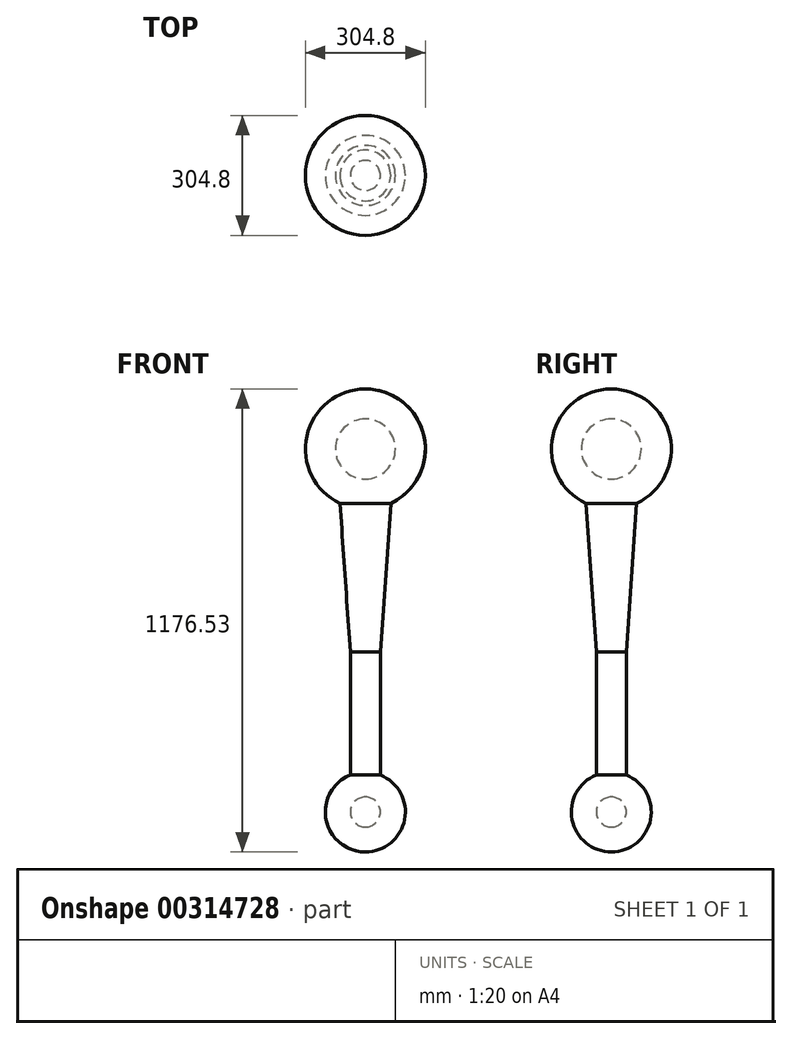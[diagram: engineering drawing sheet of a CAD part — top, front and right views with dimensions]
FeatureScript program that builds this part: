
annotation { "Feature Type Name" : "Feature", "Feature Type Description" : "" }
export const myFeature = defineFeature(function(context is Context, id is Id, definition is map)
    precondition{}
    {
        {
            var Q0;
            Q0=qCreatedBy(makeId("Front.planeOp"),FACE);
            var sketch = newSketch(context, id + "F0", { "sketchPlane" : qUnion([Q0])});
            skLineSegment(sketch, "E0", {"start": v(37.66, 184.96) * mm, "end": v(37.66, -183.34) * mm});
            skCircle(sketch, "E1", {"center": v(37.66, -221.44) * mm, "radius": 38.1 * mm});
            skLineSegment(sketch, "E2.0", {"start": v(75.76, 184.96) * mm, "end": v(75.76, -127.25) * mm});
            skArc(sketch, "E3", {"start": v(102.16, 563.01) * mm, "mid": v(186.44, 734.12) * mm, "end": v(37.66, 853.49) * mm});
            skCircle(sketch, "E4", {"center": v(37.66, 701.09) * mm, "radius": 76.2 * mm});
            skLineSegment(sketch, "E5", {"start": v(37.66, -259.54) * mm, "end": v(37.66, -323.04) * mm});
            skArc(sketch, "E6.trimOffspring", {"start": v(37.66, -323.04) * mm, "mid": v(137.39, -240.84) * mm, "end": v(75.76, -127.25) * mm});
            skLineSegment(sketch, "E7.trimOffspring", {"start": v(102.16, 563.01) * mm, "end": v(75.76, 184.96) * mm});
            skLineSegment(sketch, "E8.trimOffspring", {"start": v(37.66, 777.29) * mm, "end": v(37.66, 853.49) * mm});
            skLineSegment(sketch, "E9", {"start": v(37.66, 184.96) * mm, "end": v(37.66, 624.89) * mm});
            skSolve(sketch);
        }
        {
            var Q0;
            {var subQ1=sQuery(id+"F0.wireOp",EDGE,"E0");Q0=makeQuery(id+"F0.imprint","IMPRINT",FACE,{"disambiguationData":[TD([[makeQuery(id+"F0.imprint","IMPRINT",EDGE,{"derivedFrom":subQ1}),1.0]])]});}
            var Q1;
            Q1=sQuery(id+"F0.wireOp",EDGE,"E9");
            revolve(context, id + "F1", {"entities" : qUnion([Q0]), "axis" : qUnion([Q1]), "revolveType" : RevolveType.FULL});
        }
    });
